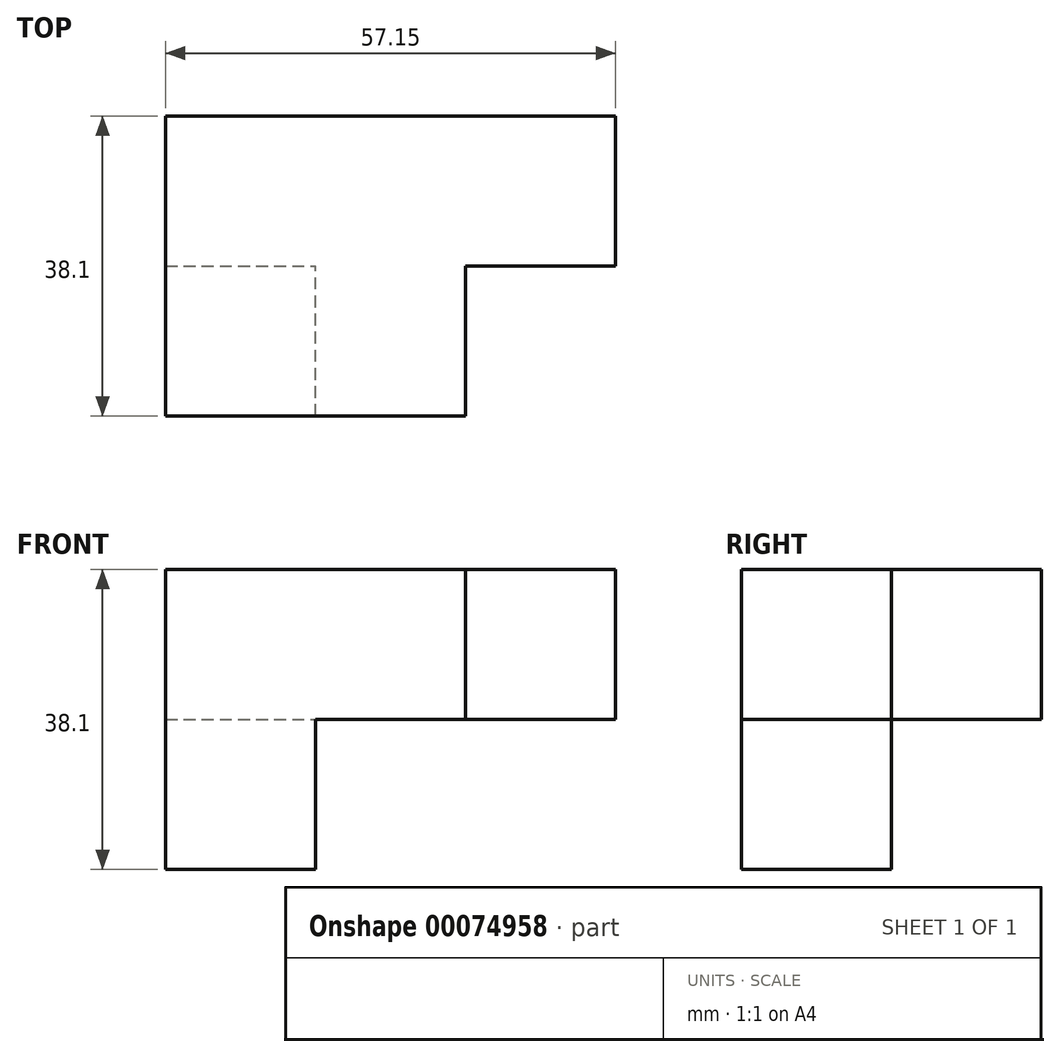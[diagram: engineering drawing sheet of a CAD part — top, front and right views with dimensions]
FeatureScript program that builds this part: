
annotation { "Feature Type Name" : "Feature", "Feature Type Description" : "" }
export const myFeature = defineFeature(function(context is Context, id is Id, definition is map)
    precondition{}
    {
        {
            var Q0;
            Q0=qCreatedBy(makeId("Front.planeOp"),FACE);
            var sketch = newSketch(context, id + "F0", { "sketchPlane" : qUnion([Q0])});
            skLineSegment(sketch, "E0.bottom", {"start": v(0, 0) * mm, "end": v(-57.15, 0) * mm});
            skLineSegment(sketch, "E0.top", {"start": v(0, 19.05) * mm, "end": v(-57.15, 19.05) * mm});
            skLineSegment(sketch, "E0.left", {"start": v(0, 0) * mm, "end": v(0, 19.05) * mm});
            skLineSegment(sketch, "E0.right", {"start": v(-57.15, 0) * mm, "end": v(-57.15, 19.05) * mm});
            skSolve(sketch);
        }
        {
            var Q0;
            Q0=qSketchRegion(id+"F0",true);
            extrude(context, id + "F1", {"entities" : qUnion([Q0]), "depth" : 19.05 * mm});
        }
        {
            var Q0;
            Q0=makeQuery(id+"F1.opExtrude","CAP_FACE",FACE,{"disambiguationData":[OSD([sQuery(id+"F0.wireOp",EDGE,"E0.bottom"),sQuery(id+"F0.wireOp",EDGE,"E0.top"),sQuery(id+"F0.wireOp",EDGE,"E0.left"),sQuery(id+"F0.wireOp",EDGE,"E0.right")])],"isStart":false});
            var sketch = newSketch(context, id + "F2", { "sketchPlane" : qUnion([Q0])});
            skLineSegment(sketch, "E1.bottom", {"start": v(-57.15, 19.05) * mm, "end": v(-19.05, 19.05) * mm});
            skLineSegment(sketch, "E1.top", {"start": v(-57.15, 0) * mm, "end": v(-19.05, 0) * mm});
            skLineSegment(sketch, "E1.left", {"start": v(-57.15, 19.05) * mm, "end": v(-57.15, 0) * mm});
            skLineSegment(sketch, "E1.right", {"start": v(-19.05, 19.05) * mm, "end": v(-19.05, 0) * mm});
            skSolve(sketch);
        }
        {
            var Q0;
            Q0=qSketchRegion(id+"F2",true);
            extrude(context, id + "F3", {"entities" : qUnion([Q0]), "operationType" : NewBodyOperationType.ADD, "depth" : 19.05 * mm});
        }
        {
            var Q0;
            Q0=makeQuery(id+"F3.boolean.opBoolean","MERGE",FACE,{"derivedFrom":[makeQuery(id+"F1.opExtrude","SWEPT_FACE",FACE,{"disambiguationData":[OSD([sQuery(id+"F0.wireOp",EDGE,"E0.bottom")])]}),makeQuery(id+"F3.opExtrude","SWEPT_FACE",FACE,{"disambiguationData":[OSD([sQuery(id+"F2.wireOp",EDGE,"E1.top")])]})]});
            var sketch = newSketch(context, id + "F4", { "sketchPlane" : qUnion([Q0])});
            skLineSegment(sketch, "E2.bottom", {"start": v(-57.15, 38.1) * mm, "end": v(-38.1, 38.1) * mm});
            skLineSegment(sketch, "E2.top", {"start": v(-57.15, 19.05) * mm, "end": v(-38.1, 19.05) * mm});
            skLineSegment(sketch, "E2.left", {"start": v(-57.15, 38.1) * mm, "end": v(-57.15, 19.05) * mm});
            skLineSegment(sketch, "E2.right", {"start": v(-38.1, 38.1) * mm, "end": v(-38.1, 19.05) * mm});
            skSolve(sketch);
        }
        {
            var Q0;
            Q0 = qSketchRegion(id + "F4", true);
            extrude(context, id + "F5", {"entities" : qUnion([Q0]), "operationType" : NewBodyOperationType.ADD, "depth" : 19.05 * mm});
        }
    });
